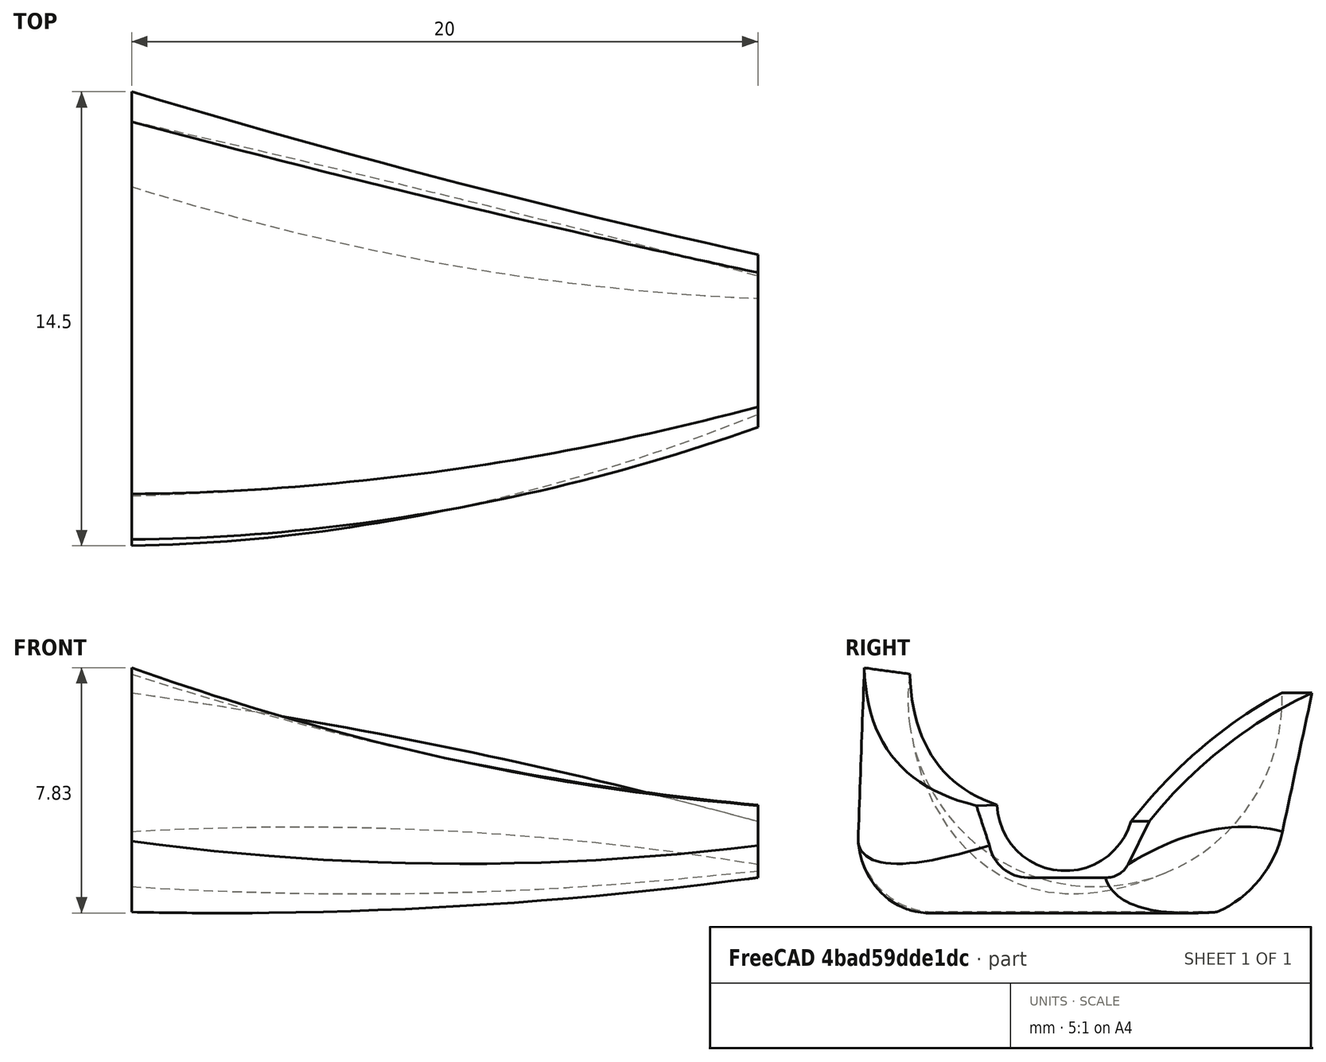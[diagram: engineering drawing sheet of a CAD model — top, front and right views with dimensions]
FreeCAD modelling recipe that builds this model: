
FCSTD DOCUMENT  (FreeCAD 0.17R13541 (Git))
Label: loft
License: All rights reserved
LicenseURL: http://en.wikipedia.org/wiki/All_rights_reserved
objects: Sketcher::SketchObject×3, PartDesign::AdditiveLoft×1, PartDesign::Body×1
note: 6 computed .brp shape members not serialized (recipe doc carries the construction recipe); baked Part::Feature solids carry a one-line shape summary decoded from their .brp

FEATURE [Sketcher::SketchObject] Sketch
  MapMode = 5
  Placement = pos=(0,0,0) rot=(0.57735,0.57735,0.57735;2.0944rad)
  Support = -> [YZ_Plane]
  sketch-geometry (8):
    g0: LineSegment StartX=-6.8 StartY=7.8 StartZ=0 EndX=-5.34809 EndY=7.6 EndZ=0
    g1: ArcOfCircle CenterX=0.57007 CenterY=6.78478 CenterZ=0 NormalX=0 NormalY=0 NormalZ=1 AngleXU=0 Radius=5.97404 StartAngle=3.0047 EndAngle=6.31922
    g2: LineSegment StartX=6.54023 StartY=7 StartZ=0 EndX=7.5 EndY=7 EndZ=0
    g3: LineSegment StartX=7.5 StartY=7 StartZ=0 EndX=6.55699 EndY=2.57361 EndZ=0
    g4: ArcOfCircle CenterX=2.99426 CenterY=3.33263 CenterZ=0 NormalX=0 NormalY=0 NormalZ=1 AngleXU=0 Radius=3.64268 StartAngle=5.12797 EndAngle=6.07328
    g5: LineSegment StartX=4.46487 StartY=0 StartZ=0 EndX=-4.52836 EndY=0 EndZ=0
    g6: ArcOfCircle CenterX=-4.52836 CenterY=2.48115 CenterZ=0 NormalX=0 NormalY=0 NormalZ=1 AngleXU=0 Radius=2.48115 StartAngle=3.22917 EndAngle=4.71239
    g7: LineSegment StartX=-7 StartY=2.26413 StartZ=0 EndX=-6.8 EndY=7.8 EndZ=0
  constraints (11):
    c: Perpendicular(g0,g1) = 4.71239
    c: Coincident(g1,g2)
    c: Horizontal(g2)
    c: Coincident(g2,g3)
    c: Tangent(g3,g4) = 1.5708
    c: Coincident(g4,g5)
    c: PointOnObject(g5,g-1)
    c: Horizontal(g5)
    c: Tangent(g5,g6) = 1.5708
    c: Coincident(g6,g7)
    c: Coincident(g7,g0)
FEATURE [Sketcher::SketchObject] Sketch001
  AttachmentOffset = pos=(0,0,10) rot=(0,0,1;0rad)
  MapMode = 5
  Placement = pos=(10,0,0) rot=(0.57735,0.57735,0.57735;2.0944rad)
  Support = -> [YZ_Plane]
  sketch-geometry (8):
    g0: LineSegment StartX=-5.86749 StartY=4.92267 StartZ=0 EndX=-4.6 EndY=4.92267 EndZ=0
    g1: ArcOfCircle CenterX=-0.292726 CenterY=4.92267 CenterZ=0 NormalX=0 NormalY=0 NormalZ=1 AngleXU=0 Radius=4.30727 StartAngle=3.14159 EndAngle=6.3654
    g2: LineSegment StartX=4 StartY=5.27638 StartZ=0 EndX=4.7 EndY=5.27638 EndZ=0
    g3: LineSegment StartX=4.7 StartY=5.27638 StartZ=0 EndX=4.2 EndY=2.6 EndZ=0
    g4: ArcOfCircle CenterX=1.10716 CenterY=3.1778 CenterZ=0 NormalX=0 NormalY=0 NormalZ=1 AngleXU=0 Radius=3.14635 StartAngle=5.00011 EndAngle=6.09849
    g5: LineSegment StartX=2 StartY=0.160791 StartZ=0 EndX=-4.3 EndY=0.160791 EndZ=0
    g6: ArcOfCircle CenterX=-4.3 CenterY=1.74051 CenterZ=0 NormalX=0 NormalY=0 NormalZ=1 AngleXU=0 Radius=1.57972 StartAngle=3.26608 EndAngle=4.71239
    g7: LineSegment StartX=-5.86749 StartY=1.54437 StartZ=0 EndX=-5.86749 EndY=4.92267 EndZ=0
  constraints (12):
    c: Horizontal(g0)
    c: Perpendicular(g0,g1) = 4.71239
    c: Coincident(g1,g2)
    c: Horizontal(g2)
    c: Coincident(g2,g3)
    c: Tangent(g3,g4) = 1.5708
    c: Coincident(g4,g5)
    c: Horizontal(g5)
    c: Tangent(g5,g6) = 1.5708
    c: Coincident(g6,g7)
    c: Coincident(g7,g0)
    c: Vertical(g7)
FEATURE [Sketcher::SketchObject] Sketch002
  AttachmentOffset = pos=(0,0,20) rot=(0,0,1;0rad)
  MapMode = 5
  Placement = pos=(20,0,0) rot=(0.57735,0.57735,0.57735;2.0944rad)
  Support = -> [YZ_Plane]
  sketch-geometry (8):
    g0: LineSegment StartX=-3.22149 StartY=3.4 StartZ=0 EndX=-2.56252 EndY=3.42325 EndZ=0
    g1: ArcOfCircle CenterX=-0.379506 CenterY=3.50026 CenterZ=0 NormalX=0 NormalY=0 NormalZ=1 AngleXU=0 Radius=2.18437 StartAngle=3.17686 EndAngle=6.00481
    g2: LineSegment StartX=1.72078 StartY=2.9 StartZ=0 EndX=2.3 EndY=2.9 EndZ=0
    g3: LineSegment StartX=2.3 StartY=2.9 StartZ=0 EndX=1.62315 EndY=1.5265 EndZ=0
    g4: ArcOfCircle CenterX=0.936137 CenterY=1.86505 CenterZ=0 NormalX=0 NormalY=0 NormalZ=1 AngleXU=0 Radius=0.765903 StartAngle=4.66519 EndAngle=5.82532
    g5: LineSegment StartX=0.9 StartY=1.1 StartZ=0 EndX=-1.57407 EndY=1.1 EndZ=0
    g6: ArcOfCircle CenterX=-1.57407 CenterY=2.34574 CenterZ=0 NormalX=0 NormalY=0 NormalZ=1 AngleXU=0 Radius=1.24574 StartAngle=3.32018 EndAngle=4.71239
    g7: LineSegment StartX=-2.8 StartY=2.12445 StartZ=0 EndX=-3.22149 EndY=3.4 EndZ=0
  constraints (10):
    c: Perpendicular(g0,g1) = 4.71239
    c: Coincident(g1,g2)
    c: Horizontal(g2)
    c: Coincident(g2,g3)
    c: Tangent(g3,g4) = 1.5708
    c: Coincident(g4,g5)
    c: Horizontal(g5)
    c: Tangent(g5,g6) = 1.5708
    c: Coincident(g6,g7)
    c: Coincident(g7,g0)
FEATURE [PartDesign::AdditiveLoft] AdditiveLoft
  Closed = false
  Placement = pos=(0,0,0) rot=(0.57735,0.57735,0.57735;2.0944rad)
  Profile = -> Sketch
  Refine = true
  Ruled = false
  Sections = -> [Sketch001,Sketch002]
FEATURE [PartDesign::Body] Body
  Group = -> [Sketch,Sketch001,Sketch002,AdditiveLoft]
  Origin = -> Origin
  Tip = -> AdditiveLoft
